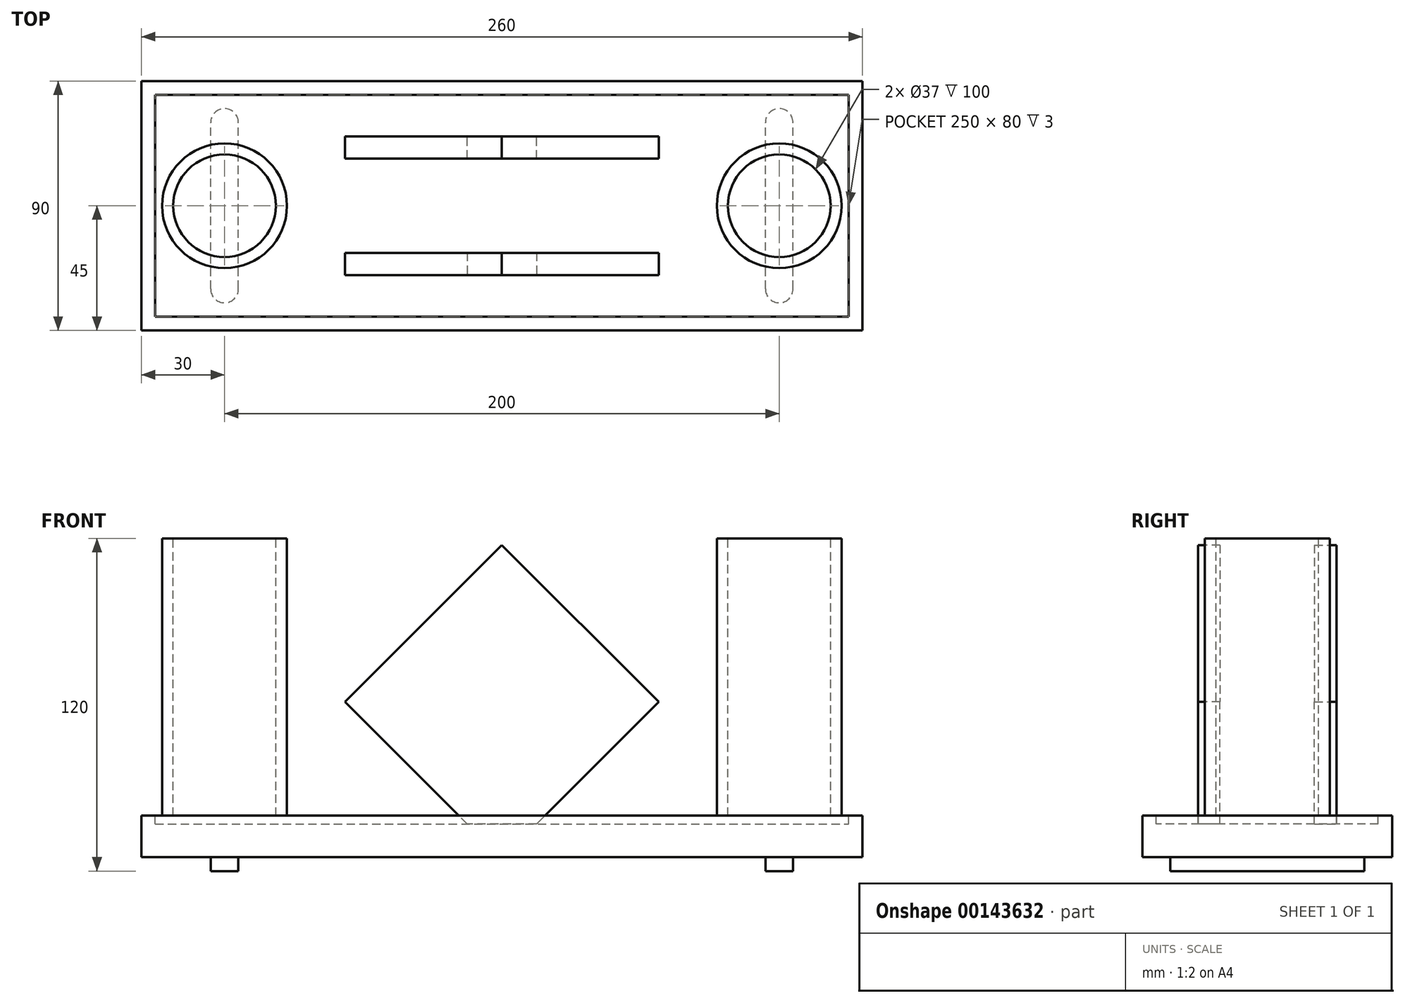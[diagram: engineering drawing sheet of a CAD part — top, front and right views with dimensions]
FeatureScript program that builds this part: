
annotation { "Feature Type Name" : "Feature", "Feature Type Description" : "" }
export const myFeature = defineFeature(function(context is Context, id is Id, definition is map)
    precondition{}
    {
        {
            var Q0;
            Q0=qCreatedBy(makeId("Top.planeOp"),FACE);
            var sketch = newSketch(context, id + "F0", { "sketchPlane" : qUnion([Q0])});
            skLineSegment(sketch, "E0.bottom", {"start": v(130, 45) * mm, "end": v(-130, 45) * mm});
            skLineSegment(sketch, "E0.top", {"start": v(130, -45) * mm, "end": v(-130, -45) * mm});
            skLineSegment(sketch, "E0.left", {"start": v(130, 45) * mm, "end": v(130, -45) * mm});
            skLineSegment(sketch, "E0.right", {"start": v(-130, 45) * mm, "end": v(-130, -45) * mm});
            skPoint(sketch, "E0.middle", {"position": v(0, 0) * mm});
            skSolve(sketch);
        }
        {
            var Q0;
            Q0 = qSketchRegion(id + "F0", true);
            extrude(context, id + "F1", {"entities" : qUnion([Q0]), "depth" : 15 * mm});
        }
        {
            var Q0;
            Q0=makeQuery(id+"F1.opExtrude","CAP_FACE",FACE,{"disambiguationData":[OSD([sQuery(id+"F0.wireOp",EDGE,"E0.bottom"),sQuery(id+"F0.wireOp",EDGE,"E0.top"),sQuery(id+"F0.wireOp",EDGE,"E0.left"),sQuery(id+"F0.wireOp",EDGE,"E0.right")])],"isStart":false});
            var sketch = newSketch(context, id + "F2", { "sketchPlane" : qUnion([Q0])});
            skCircle(sketch, "E1", {"center": v(-100, 0) * mm, "radius": 22.5 * mm});
            skCircle(sketch, "E2", {"center": v(100, 0) * mm, "radius": 22.5 * mm});
            skSolve(sketch);
        }
        {
            var Q0;
            Q0 = qSketchRegion(id + "F2", true);
            extrude(context, id + "F3", {"entities" : qUnion([Q0]), "operationType" : NewBodyOperationType.ADD, "depth" : 100 * mm});
        }
        {
            var Q0;
            Q0=makeQuery(id+"F3.opExtrude","CAP_FACE",FACE,{"disambiguationData":[OSD([sQuery(id+"F2.wireOp",EDGE,"E1")])],"isStart":false});
            var sketch = newSketch(context, id + "F4", { "sketchPlane" : qUnion([Q0])});
            skCircle(sketch, "E3", {"center": v(-100, 0) * mm, "radius": 18.5 * mm});
            skCircle(sketch, "E4", {"center": v(100, 0) * mm, "radius": 18.5 * mm});
            skSolve(sketch);
        }
        {
            var Q0;
            Q0 = qSketchRegion(id + "F4", true);
            extrude(context, id + "F5", {"entities" : qUnion([Q0]), "operationType" : NewBodyOperationType.REMOVE, "oppositeDirection" : true, "depth" : 100 * mm});
        }
        {
            var Q0;
            Q0=makeQuery(id+"F1.opExtrude","CAP_FACE",FACE,{"disambiguationData":[OSD([sQuery(id+"F0.wireOp",EDGE,"E0.bottom"),sQuery(id+"F0.wireOp",EDGE,"E0.top"),sQuery(id+"F0.wireOp",EDGE,"E0.left"),sQuery(id+"F0.wireOp",EDGE,"E0.right")])],"isStart":true});
            var sketch = newSketch(context, id + "F6", { "sketchPlane" : qUnion([Q0])});
            skLineSegment(sketch, "E5.bottom", {"start": v(-100, 35) * mm, "end": v(-100, 35) * mm});
            skLineSegment(sketch, "E5.top", {"start": v(-100, -35) * mm, "end": v(-100, -35) * mm});
            skLineSegment(sketch, "E5.left", {"start": v(-95, 30) * mm, "end": v(-95, -30) * mm});
            skLineSegment(sketch, "E5.right", {"start": v(-105, 30) * mm, "end": v(-105, -30) * mm});
            skPoint(sketch, "E5.middle", {"position": v(-100, 0) * mm});
            skLineSegment(sketch, "E6.bottom", {"start": v(100, 35) * mm, "end": v(100, 35) * mm});
            skLineSegment(sketch, "E6.top", {"start": v(100, -35) * mm, "end": v(100, -35) * mm});
            skLineSegment(sketch, "E6.left", {"start": v(105, 30) * mm, "end": v(105, -30) * mm});
            skLineSegment(sketch, "E6.right", {"start": v(95, 30) * mm, "end": v(95, -30) * mm});
            skPoint(sketch, "E6.middle", {"position": v(100, 0) * mm});
            skPoint(sketch, "E7.visualSharp", {"position": v(-105, 35) * mm});
            skArc(sketch, "E7.filletArc", {"start": v(-100, 35) * mm, "mid": v(-103.54, 33.54) * mm, "end": v(-105, 30) * mm});
            skPoint(sketch, "E8.visualSharp", {"position": v(-95, 35) * mm});
            skArc(sketch, "E8.filletArc", {"start": v(-95, 30) * mm, "mid": v(-96.46, 33.54) * mm, "end": v(-100, 35) * mm});
            skPoint(sketch, "E9.visualSharp", {"position": v(-105, -35) * mm});
            skArc(sketch, "E9.filletArc", {"start": v(-105, -30) * mm, "mid": v(-103.54, -33.54) * mm, "end": v(-100, -35) * mm});
            skPoint(sketch, "E10.visualSharp", {"position": v(-95, -35) * mm});
            skArc(sketch, "E10.filletArc", {"start": v(-100, -35) * mm, "mid": v(-96.46, -33.54) * mm, "end": v(-95, -30) * mm});
            skPoint(sketch, "E11.visualSharp", {"position": v(95, 35) * mm});
            skArc(sketch, "E11.filletArc", {"start": v(100, 35) * mm, "mid": v(96.46, 33.54) * mm, "end": v(95, 30) * mm});
            skPoint(sketch, "E12.visualSharp", {"position": v(105, 35) * mm});
            skArc(sketch, "E12.filletArc", {"start": v(105, 30) * mm, "mid": v(103.54, 33.54) * mm, "end": v(100, 35) * mm});
            skPoint(sketch, "E13.visualSharp", {"position": v(95, -35) * mm});
            skArc(sketch, "E13.filletArc", {"start": v(95, -30) * mm, "mid": v(96.46, -33.54) * mm, "end": v(100, -35) * mm});
            skPoint(sketch, "E14.visualSharp", {"position": v(105, -35) * mm});
            skArc(sketch, "E14.filletArc", {"start": v(100, -35) * mm, "mid": v(103.54, -33.54) * mm, "end": v(105, -30) * mm});
            skSolve(sketch);
        }
        {
            var Q0;
            Q0 = qSketchRegion(id + "F6", true);
            extrude(context, id + "F7", {"entities" : qUnion([Q0]), "operationType" : NewBodyOperationType.ADD, "depth" : 5 * mm});
        }
        {
            var Q0;
            Q0=makeQuery(id+"F1.opExtrude","CAP_FACE",FACE,{"disambiguationData":[OSD([sQuery(id+"F0.wireOp",EDGE,"E0.bottom"),sQuery(id+"F0.wireOp",EDGE,"E0.top"),sQuery(id+"F0.wireOp",EDGE,"E0.left"),sQuery(id+"F0.wireOp",EDGE,"E0.right")])],"isStart":false});
            var sketch = newSketch(context, id + "F8", { "sketchPlane" : qUnion([Q0])});
            skLineSegment(sketch, "E15.bottom", {"start": v(-125, 40) * mm, "end": v(125, 40) * mm});
            skLineSegment(sketch, "E15.top", {"start": v(-125, -40) * mm, "end": v(125, -40) * mm});
            skLineSegment(sketch, "E15.left", {"start": v(-125, 40) * mm, "end": v(-125, -40) * mm});
            skLineSegment(sketch, "E15.right", {"start": v(125, 40) * mm, "end": v(125, -40) * mm});
            skPoint(sketch, "E15.middle", {"position": v(0, 0) * mm});
            skSolve(sketch);
        }
        {
            var Q0;
            Q0 = qSketchRegion(id + "F8", true);
            extrude(context, id + "F9", {"entities" : qUnion([Q0]), "operationType" : NewBodyOperationType.REMOVE, "oppositeDirection" : true, "depth" : 3 * mm});
        }
        {
            var Q0;
            Q0=qCreatedBy(makeId("Front.planeOp"),FACE);
            cPlane(context, id + "F10", {"entities" : qUnion([Q0]), "cplaneType" : CPlaneType.OFFSET, "offset" : 25 * mm, "width" : 150 * mm, "height" : 150 * mm});
        }
        {
            var Q0;
            Q0=qCreatedBy(makeId("Front.planeOp"),FACE);
            cPlane(context, id + "F11", {"entities" : qUnion([Q0]), "cplaneType" : CPlaneType.OFFSET, "offset" : 25 * mm, "oppositeDirection" : true, "width" : 150 * mm, "height" : 150 * mm});
        }
        {
            var Q0;
            Q0=qCreatedBy(id+"F10.planeOp",FACE);
            var sketch = newSketch(context, id + "F12", { "sketchPlane" : qUnion([Q0])});
            skCircle(sketch, "E16.cCircle", {"center": v(0, 56.01) * mm, "radius": 56.57 * mm, "construction": true});
            skLineSegment(sketch, "E16.0", {"start": v(-12.56, 12) * mm, "end": v(-56.57, 56.01) * mm});
            skLineSegment(sketch, "E16.1", {"start": v(-56.57, 56.01) * mm, "end": v(0, 112.58) * mm});
            skLineSegment(sketch, "E16.2", {"start": v(0, 112.58) * mm, "end": v(56.57, 56.01) * mm});
            skLineSegment(sketch, "E16.3", {"start": v(56.57, 56.01) * mm, "end": v(12.56, 12) * mm});
            skLineSegment(sketch, "E17", {"start": v(-12.56, 12) * mm, "end": v(12.56, 12) * mm});
            skPoint(sketch, "E18.orphan", {"position": v(0, -0.56) * mm});
            skSolve(sketch);
        }
        {
            var Q0;
            Q0 = qSketchRegion(id + "F12", true);
            extrude(context, id + "F13", {"entities" : qUnion([Q0]), "oppositeDirection" : true, "depth" : 8 * mm});
        }
        {
            var Q0;
            Q0=qCreatedBy(id+"F11.planeOp",FACE);
            var sketch = newSketch(context, id + "F14", { "sketchPlane" : qUnion([Q0])});
            skCircle(sketch, "E19.cCircle", {"center": v(0, 56.01) * mm, "radius": 56.57 * mm, "construction": true});
            skLineSegment(sketch, "E19.0", {"start": v(-12.56, 12) * mm, "end": v(-56.57, 56.01) * mm});
            skLineSegment(sketch, "E19.1", {"start": v(-56.57, 56.01) * mm, "end": v(0, 112.58) * mm});
            skLineSegment(sketch, "E19.2", {"start": v(0, 112.58) * mm, "end": v(56.57, 56.01) * mm});
            skLineSegment(sketch, "E19.3", {"start": v(56.57, 56.01) * mm, "end": v(12.56, 12) * mm});
            skLineSegment(sketch, "E20", {"start": v(12.56, 12) * mm, "end": v(-12.56, 12) * mm});
            skPoint(sketch, "E21.orphan", {"position": v(0, -0.56) * mm});
            skSolve(sketch);
        }
        {
            var Q0;
            Q0 = qSketchRegion(id + "F14", true);
            extrude(context, id + "F15", {"entities" : qUnion([Q0]), "depth" : 8 * mm});
        }
    });
